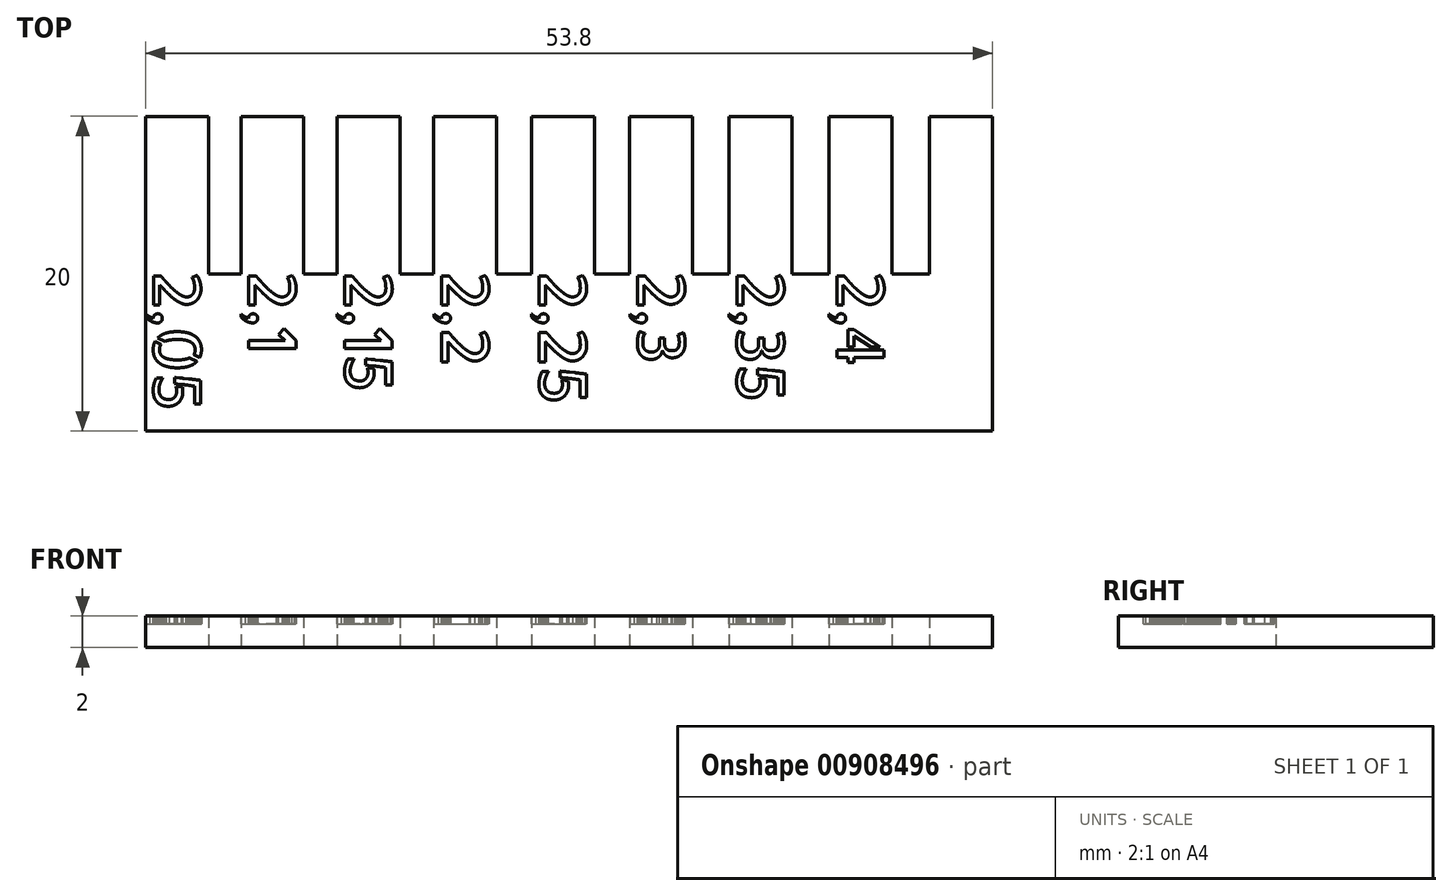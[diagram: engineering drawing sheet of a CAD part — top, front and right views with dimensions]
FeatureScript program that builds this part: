
annotation { "Feature Type Name" : "Feature", "Feature Type Description" : "" }
export const myFeature = defineFeature(function(context is Context, id is Id, definition is map)
    precondition{}
    {
        {
            var Q0;
            Q0=qCreatedBy(makeId("Top.planeOp"),FACE);
            var sketch = newSketch(context, id + "F0", { "sketchPlane" : qUnion([Q0])});
            skLineSegment(sketch, "E0.bottom", {"start": v(-49.33, 32.06) * mm, "end": v(-45.33, 32.06) * mm});
            skLineSegment(sketch, "E0.top", {"start": v(-49.33, 12.06) * mm, "end": v(-1.58, 12.06) * mm});
            skLineSegment(sketch, "E0.left", {"start": v(-49.33, 22.06) * mm, "end": v(-49.33, 12.06) * mm, "construction": true});
            skLineSegment(sketch, "E1.9.0.0", {"start": v(-1.58, 32.06) * mm, "end": v(-1.58, 12.06) * mm});
            skLineSegment(sketch, "E2.0", {"start": v(-45.33, 22.06) * mm, "end": v(-45.33, 12.06) * mm, "construction": true});
            skLineSegment(sketch, "E3.MirrorCS", {"start": v(-43.23, 22.06) * mm, "end": v(-43.23, 12.06) * mm, "construction": true});
            skLineSegment(sketch, "E4.0", {"start": v(-39.23, 22.06) * mm, "end": v(-39.23, 12.06) * mm, "construction": true});
            skLineSegment(sketch, "E5.MirrorCS", {"start": v(-37.08, 22.06) * mm, "end": v(-37.08, 12.06) * mm, "construction": true});
            skLineSegment(sketch, "E6.0", {"start": v(-33.08, 22.06) * mm, "end": v(-33.08, 12.06) * mm, "construction": true});
            skLineSegment(sketch, "E7.MirrorCS", {"start": v(-30.88, 22.06) * mm, "end": v(-30.88, 12.06) * mm, "construction": true});
            skLineSegment(sketch, "E8.0", {"start": v(-26.88, 22.06) * mm, "end": v(-26.88, 12.06) * mm, "construction": true});
            skLineSegment(sketch, "E9.MirrorCS", {"start": v(-24.63, 22.06) * mm, "end": v(-24.63, 12.06) * mm, "construction": true});
            skLineSegment(sketch, "E10.0", {"start": v(-20.63, 22.06) * mm, "end": v(-20.63, 12.06) * mm, "construction": true});
            skLineSegment(sketch, "E11.MirrorCS", {"start": v(-18.33, 22.06) * mm, "end": v(-18.33, 12.06) * mm, "construction": true});
            skLineSegment(sketch, "E12.0", {"start": v(-14.33, 22.06) * mm, "end": v(-14.33, 12.06) * mm, "construction": true});
            skLineSegment(sketch, "E13.MirrorCS", {"start": v(-11.98, 22.06) * mm, "end": v(-11.98, 12.06) * mm, "construction": true});
            skLineSegment(sketch, "E14.0", {"start": v(-7.98, 22.06) * mm, "end": v(-7.98, 12.06) * mm, "construction": true});
            skLineSegment(sketch, "E15.MirrorCS", {"start": v(-5.58, 22.06) * mm, "end": v(-5.58, 12.06) * mm, "construction": true});
            skLineSegment(sketch, "E16", {"start": v(-45.33, 22.06) * mm, "end": v(-43.23, 22.06) * mm});
            skLineSegment(sketch, "E17.trimOffspring", {"start": v(-39.23, 22.06) * mm, "end": v(-37.08, 22.06) * mm});
            skLineSegment(sketch, "E18.trimOffspring", {"start": v(-33.08, 22.06) * mm, "end": v(-30.88, 22.06) * mm});
            skLineSegment(sketch, "E19.trimOffspring", {"start": v(-26.88, 22.06) * mm, "end": v(-24.63, 22.06) * mm});
            skLineSegment(sketch, "E20.trimOffspring", {"start": v(-20.63, 22.06) * mm, "end": v(-18.33, 22.06) * mm});
            skLineSegment(sketch, "E21.trimOffspring", {"start": v(-14.33, 22.06) * mm, "end": v(-11.98, 22.06) * mm});
            skLineSegment(sketch, "E22.trimOffspring", {"start": v(-7.98, 22.06) * mm, "end": v(-5.58, 22.06) * mm});
            skLineSegment(sketch, "E23.trimOffspring", {"start": v(-43.23, 32.06) * mm, "end": v(-39.23, 32.06) * mm});
            skLineSegment(sketch, "E24.trimOffspring", {"start": v(-37.08, 32.06) * mm, "end": v(-33.08, 32.06) * mm});
            skLineSegment(sketch, "E25.trimOffspring", {"start": v(-30.88, 32.06) * mm, "end": v(-26.88, 32.06) * mm});
            skLineSegment(sketch, "E26.trimOffspring", {"start": v(-24.63, 32.06) * mm, "end": v(-20.63, 32.06) * mm});
            skLineSegment(sketch, "E27.trimOffspring", {"start": v(-18.33, 32.06) * mm, "end": v(-14.33, 32.06) * mm});
            skLineSegment(sketch, "E28.trimOffspring", {"start": v(-11.98, 32.06) * mm, "end": v(-7.98, 32.06) * mm});
            skLineSegment(sketch, "E29.trimOffspring", {"start": v(-5.58, 32.06) * mm, "end": v(-1.58, 32.06) * mm});
            skLineSegment(sketch, "E30.0", {"start": v(-51.38, 22.06) * mm, "end": v(-51.38, 12.06) * mm, "construction": true});
            skLineSegment(sketch, "E31.bottom", {"start": v(-55.38, 32.06) * mm, "end": v(-51.38, 32.06) * mm});
            skLineSegment(sketch, "E32", {"start": v(-55.38, 32.06) * mm, "end": v(-55.38, 12.06) * mm});
            skLineSegment(sketch, "E33", {"start": v(-55.38, 12.06) * mm, "end": v(-49.33, 12.06) * mm});
            skLineSegment(sketch, "E34", {"start": v(-51.38, 22.06) * mm, "end": v(-49.33, 22.06) * mm});
            skLineSegment(sketch, "E35", {"start": v(-51.38, 22.06) * mm, "end": v(-51.38, 32.06) * mm});
            skLineSegment(sketch, "E36", {"start": v(-49.33, 22.06) * mm, "end": v(-49.33, 32.06) * mm});
            skLineSegment(sketch, "E37", {"start": v(-45.33, 22.06) * mm, "end": v(-45.33, 32.06) * mm});
            skLineSegment(sketch, "E38", {"start": v(-43.23, 22.06) * mm, "end": v(-43.23, 32.06) * mm});
            skLineSegment(sketch, "E39", {"start": v(-39.23, 22.06) * mm, "end": v(-39.23, 32.06) * mm});
            skLineSegment(sketch, "E40", {"start": v(-37.08, 22.06) * mm, "end": v(-37.08, 32.06) * mm});
            skLineSegment(sketch, "E41", {"start": v(-33.08, 22.06) * mm, "end": v(-33.08, 32.06) * mm});
            skLineSegment(sketch, "E42", {"start": v(-30.88, 22.06) * mm, "end": v(-30.88, 32.06) * mm});
            skLineSegment(sketch, "E43", {"start": v(-26.88, 22.06) * mm, "end": v(-26.88, 32.06) * mm});
            skLineSegment(sketch, "E44", {"start": v(-24.63, 22.06) * mm, "end": v(-24.63, 32.06) * mm});
            skLineSegment(sketch, "E45", {"start": v(-20.63, 22.06) * mm, "end": v(-20.63, 32.06) * mm});
            skLineSegment(sketch, "E46", {"start": v(-18.33, 22.06) * mm, "end": v(-18.33, 32.06) * mm});
            skLineSegment(sketch, "E47", {"start": v(-14.33, 22.06) * mm, "end": v(-14.33, 32.06) * mm});
            skLineSegment(sketch, "E48", {"start": v(-11.98, 22.06) * mm, "end": v(-11.98, 32.06) * mm});
            skLineSegment(sketch, "E49", {"start": v(-7.98, 22.06) * mm, "end": v(-7.98, 32.06) * mm});
            skLineSegment(sketch, "E50", {"start": v(-5.58, 22.06) * mm, "end": v(-5.58, 32.06) * mm});
            skSolve(sketch);
        }
        {
            var Q0;
            Q0=makeQuery(id+"F0.imprint","IMPRINT",FACE,{"disambiguationData":[TD([[makeQuery(id+"F0.imprint","IMPRINT",EDGE,{"derivedFrom":sQuery(id+"F0.wireOp",EDGE,"E0.bottom")}),-1.0]])]});
            extrude(context, id + "F1", {"entities" : qUnion([Q0]), "depth" : 2 * mm, "offsetDistance" : 25 * mm});
        }
        {
            var Q0;
            Q0=makeQuery(id+"F1.opExtrude","CAP_FACE",FACE,{"disambiguationData":[OSD([sQuery(id+"F0.wireOp",EDGE,"E0.bottom"),sQuery(id+"F0.wireOp",EDGE,"E0.top"),sQuery(id+"F0.wireOp",EDGE,"E1.9.0.0"),sQuery(id+"F0.wireOp",EDGE,"E16"),sQuery(id+"F0.wireOp",EDGE,"E17.trimOffspring"),sQuery(id+"F0.wireOp",EDGE,"E18.trimOffspring"),sQuery(id+"F0.wireOp",EDGE,"E19.trimOffspring"),sQuery(id+"F0.wireOp",EDGE,"E20.trimOffspring"),sQuery(id+"F0.wireOp",EDGE,"E21.trimOffspring"),sQuery(id+"F0.wireOp",EDGE,"E22.trimOffspring"),sQuery(id+"F0.wireOp",EDGE,"E23.trimOffspring"),sQuery(id+"F0.wireOp",EDGE,"E24.trimOffspring"),sQuery(id+"F0.wireOp",EDGE,"E25.trimOffspring"),sQuery(id+"F0.wireOp",EDGE,"E26.trimOffspring"),sQuery(id+"F0.wireOp",EDGE,"E27.trimOffspring"),sQuery(id+"F0.wireOp",EDGE,"E28.trimOffspring"),sQuery(id+"F0.wireOp",EDGE,"E29.trimOffspring"),sQuery(id+"F0.wireOp",EDGE,"E31.bottom"),sQuery(id+"F0.wireOp",EDGE,"E32"),sQuery(id+"F0.wireOp",EDGE,"E33"),sQuery(id+"F0.wireOp",EDGE,"E34"),sQuery(id+"F0.wireOp",EDGE,"E35"),sQuery(id+"F0.wireOp",EDGE,"E36"),sQuery(id+"F0.wireOp",EDGE,"E37"),sQuery(id+"F0.wireOp",EDGE,"E38"),sQuery(id+"F0.wireOp",EDGE,"E39"),sQuery(id+"F0.wireOp",EDGE,"E40"),sQuery(id+"F0.wireOp",EDGE,"E41"),sQuery(id+"F0.wireOp",EDGE,"E42"),sQuery(id+"F0.wireOp",EDGE,"E43"),sQuery(id+"F0.wireOp",EDGE,"E44"),sQuery(id+"F0.wireOp",EDGE,"E45"),sQuery(id+"F0.wireOp",EDGE,"E46"),sQuery(id+"F0.wireOp",EDGE,"E47"),sQuery(id+"F0.wireOp",EDGE,"E48"),sQuery(id+"F0.wireOp",EDGE,"E49"),sQuery(id+"F0.wireOp",EDGE,"E50")])],"isStart":false});
            var sketch = newSketch(context, id + "F2", { "sketchPlane" : qUnion([Q0])});
            skText(sketch, "E51", { "text": "2,05", "fontName": "AllertaStencil-Regular.ttf"});
            skText(sketch, "E52", { "text": "2,1", "fontName": "AllertaStencil-Regular.ttf"});
            skText(sketch, "E53", { "text": "2,15", "fontName": "AllertaStencil-Regular.ttf"});
            skText(sketch, "E54", { "text": "2,2", "fontName": "AllertaStencil-Regular.ttf"});
            skText(sketch, "E55", { "text": "2,25", "fontName": "AllertaStencil-Regular.ttf"});
            skText(sketch, "E56", { "text": "2,3", "fontName": "AllertaStencil-Regular.ttf"});
            skText(sketch, "E57", { "text": "2,35", "fontName": "AllertaStencil-Regular.ttf"});
            skText(sketch, "E58", { "text": "2,4", "fontName": "AllertaStencil-Regular.ttf"});
            const initialGuessF2  = {"E51": [-0.05488, 0.02228, 0, -1, 0.003], "E52": [-0.04883, 0.02228, 0, -1, 0.003], "E53": [-0.04273, 0.02228, 0, -1, 0.003], "E54": [-0.03658, 0.02228, 0, -1, 0.003], "E55": [-0.03038, 0.02228, 0, -1, 0.003], "E56": [-0.02413, 0.02228, 0, -1, 0.003], "E57": [-0.01783, 0.02228, 0, -1, 0.003], "E58": [-0.01148, 0.02228, 0, -1, 0.003]};
            skSetInitialGuess(sketch, initialGuessF2);
            skSolve(sketch);
        }
        {
            var Q0;
            Q0 = qSketchRegion(id + "F2", true);
            extrude(context, id + "F3", {"entities" : qUnion([Q0]), "operationType" : NewBodyOperationType.REMOVE, "oppositeDirection" : true, "depth" : 0.5 * mm, "offsetDistance" : 25 * mm});
        }
    });
